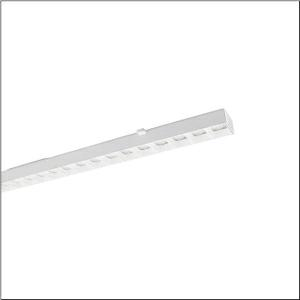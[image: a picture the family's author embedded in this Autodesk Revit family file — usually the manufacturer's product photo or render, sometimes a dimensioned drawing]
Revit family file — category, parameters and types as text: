
# Revit family: silica_r__31_fur_modario_r__31_51ry19mb46c_4938
name_source: partatom
category: Lighting Fixtures
units: mm (PartAtom-declared; Revit-internal decimal feet)

## family parameters
Cut with Voids When Loaded = No
Host = Face
Light Source = No
Part Type = Normal
Room Calculation Point = No
Round Connector Dimension = Use Diameter
Shared = No

## types (1)
- --- (1 x LED, 6620 lm, 37.8 W, 4000K)
    Apparent Load = 38 VA
    CIE Flux Codes = 72 95 99 100 100
    Color Rendering = 80
    Color Temperature = 4000K
    Default Elevation = 1800 mm
    Description = Silica® 31 for Modario® 31, luminaire insert, of aluminium, coated, traffic white (RAL 9016), length: 1.495mm, width: 79mm, height: 62mm, 5x system unit, system units: 299mm, LED rated luminous flux: 6.620lm, light colour: 840, control gear: ON/OFF Multilumen, with system connector: socket, mains connection: 220..240V, AC, 50/60Hz, rated input power: 38W, luminous flux adjustable on luminaire in four steps (3850/4650/5610/6620lm), connected load according to luminous flux setting (21.7/26.3/31.8/37.8W), primary light control with lens, of PMMA, primary anti-glare with reflector, of PC, light emission: direct distribution, primary light characteristic: double asymmetric, protection rating (complete): IP20, insulation class (complete): insulation class I (protective earthing), certification: CE, UKCA, impact resistance: IK02, permissible ambient temperature for indoor applications: -20..+40°C, LABS conformity tested according to VDMA 24364:2018-05, packaging unit: 1 piece
    Height = 62 mm  [stored 0.203412 ft]
    Lamp = 1 x LED
    Lamp Light Flux = 6620 lm
    Lamp Power = 37.8 W
    Lamp count = 1
    Length = 1495 mm
    Luminous efficacy = 175 lm/W
    Manufacturer = Siteco
    ModVariant = No
    Model = 51RY19MB46C
    Mounting Place = Ceiling
    Mounting Type = Pendant
    Number of Poles = 1
    OnlyDefault = Yes
    Power Factor = 1
    Product Name = Silica® 31 für Modario® 31
    Product group = luminaire insert
    ProductGroupID = 901
    Protection Class = Protection class I
    Protection Degree = IP 20
    RLX_Detail_Level = 1
    RLX_Emergency_Light_Flux = 0 lm
    RLX_Emergency_Type = 0
    RLX_Emergency_Type_DB = No
    RlxData = <blob elided: 14097 chars, md5=90e6ea7a>
    Socket = socket
    Standby Power = 0 W
    System Light Flux = 6620 lm
    System Power = 38 W
    Type Comments = factory setting: luminous flux: 100 % | (OFF | OFF | OFF) | 350 mA
    Type Image = l_1299352.jpg
    URL = http://relux.com
    VarID = @adj_017221
    Voltage = 0 V
    Weight = 0.00 kg
    Width = 79 mm

note: [stored X ft] marks values corroborated as IEEE doubles in the binary element streams (Revit-internal decimal feet)

## geometry (parser evidence)
native form markers: Sweep x11
no freeform markers — native parametric forms only
